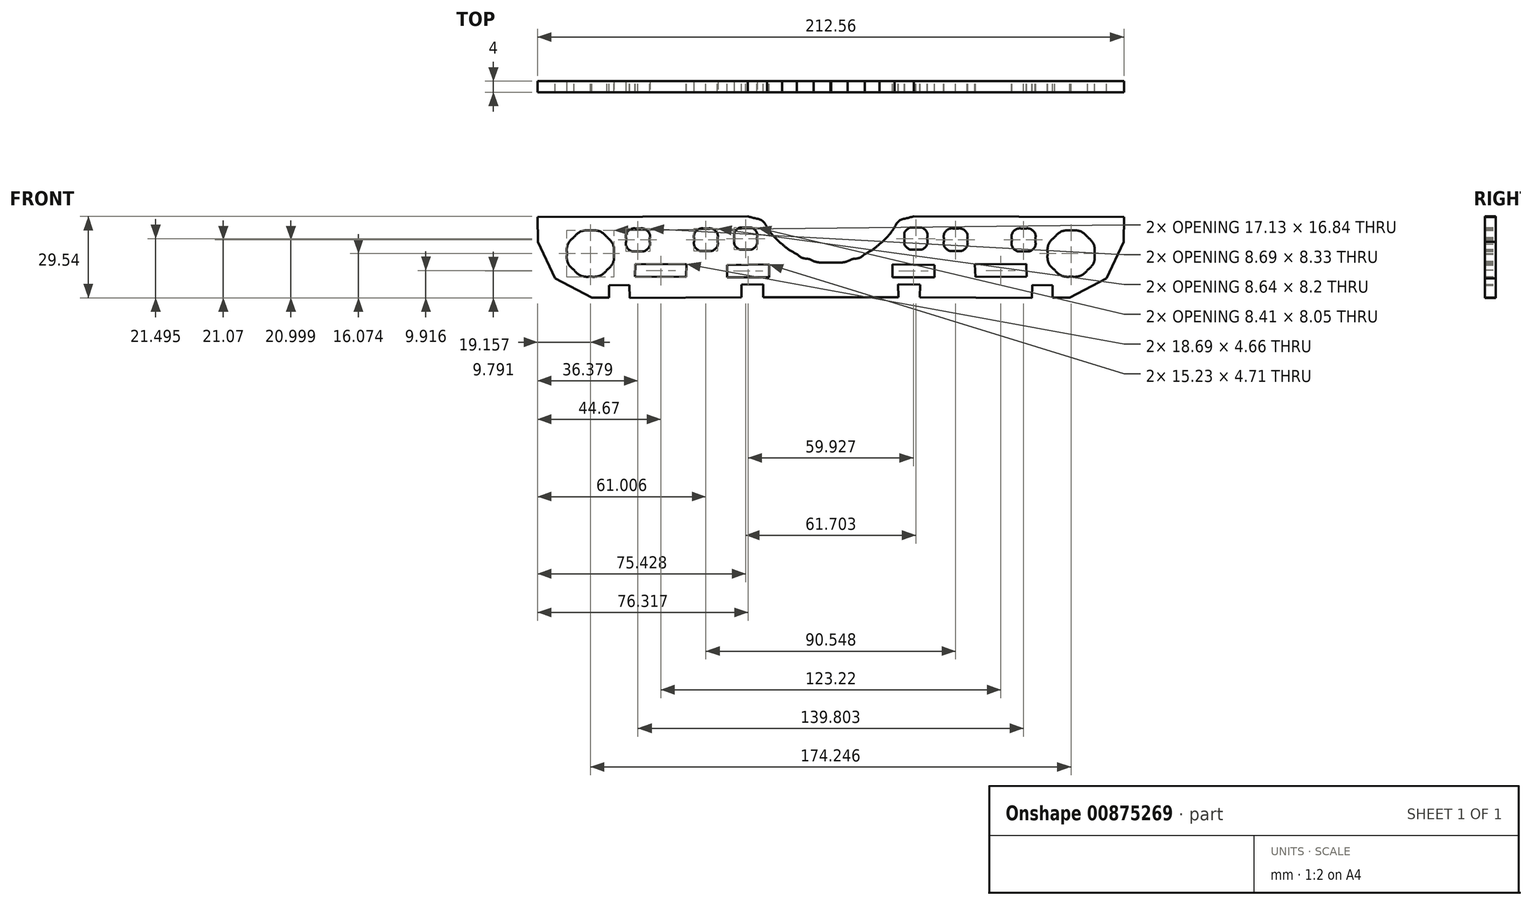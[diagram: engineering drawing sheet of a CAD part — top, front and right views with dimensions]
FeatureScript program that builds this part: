
annotation { "Feature Type Name" : "Feature", "Feature Type Description" : "" }
export const myFeature = defineFeature(function(context is Context, id is Id, definition is map)
    precondition{}
    {
        {
            var Q0;
            Q0=qCreatedBy(makeId("Front.planeOp"),FACE);
            var sketch = newSketch(context, id + "F0", { "sketchPlane" : qUnion([Q0])});
            skLineSegment(sketch, "E0", {"start": v(30.11, 14.14) * mm, "end": v(106.28, 13.9) * mm});
            skLineSegment(sketch, "E1", {"start": v(106.28, 13.9) * mm, "end": v(106.17, 4.91) * mm});
            skLineSegment(sketch, "E2", {"start": v(106.17, 4.91) * mm, "end": v(99.97, -8.35) * mm});
            skLineSegment(sketch, "E3", {"start": v(99.97, -8.35) * mm, "end": v(86.64, -15.33) * mm});
            skLineSegment(sketch, "E4", {"start": v(86.64, -15.33) * mm, "end": v(80.43, -15.33) * mm});
            skLineSegment(sketch, "E5", {"start": v(80.43, -15.33) * mm, "end": v(80.4, -10.83) * mm});
            skLineSegment(sketch, "E6", {"start": v(80.4, -10.83) * mm, "end": v(72.99, -10.77) * mm});
            skLineSegment(sketch, "E7", {"start": v(72.99, -10.77) * mm, "end": v(72.93, -15.4) * mm});
            skLineSegment(sketch, "E8", {"start": v(72.93, -15.4) * mm, "end": v(32.32, -15.13) * mm});
            skLineSegment(sketch, "E9", {"start": v(32.32, -15.13) * mm, "end": v(32.37, -10.57) * mm});
            skLineSegment(sketch, "E10", {"start": v(32.37, -10.57) * mm, "end": v(24.47, -10.45) * mm});
            skLineSegment(sketch, "E11", {"start": v(24.47, -10.45) * mm, "end": v(24.52, -15.13) * mm});
            skLineSegment(sketch, "E12", {"start": v(24.52, -15.13) * mm, "end": v(0, -15.23) * mm});
            skLineSegment(sketch, "E13", {"start": v(22.4, -3.25) * mm, "end": v(37.58, -3.45) * mm});
            skLineSegment(sketch, "E14", {"start": v(37.58, -3.45) * mm, "end": v(37.58, -7.91) * mm});
            skLineSegment(sketch, "E15", {"start": v(37.58, -7.91) * mm, "end": v(22.35, -7.96) * mm});
            skLineSegment(sketch, "E16", {"start": v(22.35, -7.96) * mm, "end": v(22.4, -3.25) * mm});
            skLineSegment(sketch, "E17", {"start": v(52.26, -3.2) * mm, "end": v(70.9, -3.15) * mm});
            skLineSegment(sketch, "E18", {"start": v(70.9, -3.15) * mm, "end": v(70.96, -7.71) * mm});
            skLineSegment(sketch, "E19", {"start": v(70.96, -7.71) * mm, "end": v(52.41, -7.81) * mm});
            skLineSegment(sketch, "E20", {"start": v(52.41, -7.81) * mm, "end": v(52.26, -3.2) * mm});
            skFitSpline(sketch, "E21", {"points": [v(0.1, -2.65) * mm, v(2.27, -2.62) * mm, v(4.38, -2.53) * mm, v(6.16, -2.1) * mm]});
            skFitSpline(sketch, "E22", {"points": [v(6.16, -2.1) * mm, v(8.2, -1.27) * mm, v(10.35, -0.92) * mm, v(12.27, 0.5) * mm]});
            skFitSpline(sketch, "E23", {"points": [v(12.27, 0.5) * mm, v(14.37, 1.56) * mm, v(16.13, 2.79) * mm, v(17.69, 4.11) * mm]});
            skFitSpline(sketch, "E24", {"points": [v(17.69, 4.11) * mm, v(19.77, 5.91) * mm, v(21.55, 7.93) * mm, v(23.1, 10.13) * mm]});
            skFitSpline(sketch, "E25", {"points": [v(23.1, 10.13) * mm, v(24.67, 12.45) * mm, v(27.21, 13.4) * mm, v(30.11, 14.14) * mm]});
            skFitSpline(sketch, "E26", {"points": [v(34.93, 6.1) * mm, v(34.93, 3.94) * mm, v(33.1, 2.2) * mm, v(30.85, 2.2) * mm]});
            skFitSpline(sketch, "E27", {"points": [v(30.85, 2.2) * mm, v(28.6, 2.2) * mm, v(26.78, 3.94) * mm, v(26.78, 6.1) * mm]});
            skFitSpline(sketch, "E28", {"points": [v(26.78, 6.1) * mm, v(26.78, 8.25) * mm, v(28.6, 10) * mm, v(30.85, 10) * mm]});
            skFitSpline(sketch, "E29", {"points": [v(30.85, 10) * mm, v(33.1, 10) * mm, v(34.93, 8.25) * mm, v(34.93, 6.1) * mm]});
            skFitSpline(sketch, "E30", {"points": [v(49.46, 5.67) * mm, v(49.46, 3.48) * mm, v(47.58, 1.7) * mm, v(45.27, 1.7) * mm]});
            skFitSpline(sketch, "E31", {"points": [v(45.27, 1.7) * mm, v(42.96, 1.7) * mm, v(41.1, 3.48) * mm, v(41.1, 5.67) * mm]});
            skFitSpline(sketch, "E32", {"points": [v(41.1, 5.67) * mm, v(41.1, 7.86) * mm, v(42.96, 9.64) * mm, v(45.27, 9.64) * mm]});
            skFitSpline(sketch, "E33", {"points": [v(45.27, 9.64) * mm, v(47.58, 9.64) * mm, v(49.46, 7.86) * mm, v(49.46, 5.67) * mm]});
            skFitSpline(sketch, "E34", {"points": [v(74.11, 5.6) * mm, v(74.11, 3.37) * mm, v(72.23, 1.57) * mm, v(69.9, 1.57) * mm]});
            skFitSpline(sketch, "E35", {"points": [v(69.9, 1.57) * mm, v(67.58, 1.57) * mm, v(65.7, 3.37) * mm, v(65.7, 5.6) * mm]});
            skFitSpline(sketch, "E36", {"points": [v(65.7, 5.6) * mm, v(65.7, 7.83) * mm, v(67.58, 9.63) * mm, v(69.9, 9.63) * mm]});
            skFitSpline(sketch, "E37", {"points": [v(69.9, 9.63) * mm, v(72.23, 9.63) * mm, v(74.11, 7.83) * mm, v(74.11, 5.6) * mm]});
            skFitSpline(sketch, "E38", {"points": [v(95.63, 0.67) * mm, v(95.63, -1.54) * mm, v(94.73, -3.67) * mm, v(93.14, -5.24) * mm]});
            skFitSpline(sketch, "E39", {"points": [v(93.14, -5.24) * mm, v(91.54, -6.8) * mm, v(89.38, -7.69) * mm, v(87.12, -7.69) * mm]});
            skFitSpline(sketch, "E40", {"points": [v(87.12, -7.69) * mm, v(84.87, -7.69) * mm, v(82.7, -6.8) * mm, v(81.11, -5.24) * mm]});
            skFitSpline(sketch, "E41", {"points": [v(81.11, -5.24) * mm, v(79.52, -3.67) * mm, v(78.62, -1.54) * mm, v(78.62, 0.67) * mm]});
            skFitSpline(sketch, "E42", {"points": [v(78.62, 0.67) * mm, v(78.62, 2.9) * mm, v(79.52, 5.02) * mm, v(81.11, 6.59) * mm]});
            skFitSpline(sketch, "E43", {"points": [v(81.11, 6.59) * mm, v(82.7, 8.15) * mm, v(84.87, 9.04) * mm, v(87.12, 9.04) * mm]});
            skFitSpline(sketch, "E44", {"points": [v(87.12, 9.04) * mm, v(89.38, 9.04) * mm, v(91.54, 8.15) * mm, v(93.14, 6.59) * mm]});
            skFitSpline(sketch, "E45", {"points": [v(93.14, 6.59) * mm, v(94.73, 5.02) * mm, v(95.63, 2.9) * mm, v(95.63, 0.67) * mm]});
            skLineSegment(sketch, "E46", {"start": v(0.1, -2.65) * mm, "end": v(0, -2.65) * mm});
            skLineSegment(sketch, "E47", {"start": v(0, -2.65) * mm, "end": v(0, -15.23) * mm});
            skSolve(sketch);
        }
        {
            var Q0;
            Q0 = qSketchRegion(id + "F0", true);
            extrude(context, id + "F1", {"entities" : qUnion([Q0]), "depth" : 4 * mm, "offsetDistance" : 25 * mm});
        }
        {
            var Q0;
            Q0=makeQuery(id+"F1.opExtrude","SWEPT_BODY",BODY,{"disambiguationData":[OSD([sQuery(id+"F0.wireOp",EDGE,"E0"),sQuery(id+"F0.wireOp",EDGE,"E1"),sQuery(id+"F0.wireOp",EDGE,"E2"),sQuery(id+"F0.wireOp",EDGE,"E3"),sQuery(id+"F0.wireOp",EDGE,"E4"),sQuery(id+"F0.wireOp",EDGE,"E5"),sQuery(id+"F0.wireOp",EDGE,"E6"),sQuery(id+"F0.wireOp",EDGE,"E7"),sQuery(id+"F0.wireOp",EDGE,"E8"),sQuery(id+"F0.wireOp",EDGE,"E9"),sQuery(id+"F0.wireOp",EDGE,"E10"),sQuery(id+"F0.wireOp",EDGE,"E11"),sQuery(id+"F0.wireOp",EDGE,"E12"),sQuery(id+"F0.wireOp",EDGE,"E13"),sQuery(id+"F0.wireOp",EDGE,"E14"),sQuery(id+"F0.wireOp",EDGE,"E15"),sQuery(id+"F0.wireOp",EDGE,"E16"),sQuery(id+"F0.wireOp",EDGE,"E17"),sQuery(id+"F0.wireOp",EDGE,"E18"),sQuery(id+"F0.wireOp",EDGE,"E19"),sQuery(id+"F0.wireOp",EDGE,"E20"),sQuery(id+"F0.wireOp",EDGE,"E21"),sQuery(id+"F0.wireOp",EDGE,"E22"),sQuery(id+"F0.wireOp",EDGE,"E23"),sQuery(id+"F0.wireOp",EDGE,"E24"),sQuery(id+"F0.wireOp",EDGE,"E25"),sQuery(id+"F0.wireOp",EDGE,"E26"),sQuery(id+"F0.wireOp",EDGE,"E27"),sQuery(id+"F0.wireOp",EDGE,"E28"),sQuery(id+"F0.wireOp",EDGE,"E29"),sQuery(id+"F0.wireOp",EDGE,"E30"),sQuery(id+"F0.wireOp",EDGE,"E31"),sQuery(id+"F0.wireOp",EDGE,"E32"),sQuery(id+"F0.wireOp",EDGE,"E33"),sQuery(id+"F0.wireOp",EDGE,"E34"),sQuery(id+"F0.wireOp",EDGE,"E35"),sQuery(id+"F0.wireOp",EDGE,"E36"),sQuery(id+"F0.wireOp",EDGE,"E37"),sQuery(id+"F0.wireOp",EDGE,"E38"),sQuery(id+"F0.wireOp",EDGE,"E39"),sQuery(id+"F0.wireOp",EDGE,"E40"),sQuery(id+"F0.wireOp",EDGE,"E41"),sQuery(id+"F0.wireOp",EDGE,"E42"),sQuery(id+"F0.wireOp",EDGE,"E43"),sQuery(id+"F0.wireOp",EDGE,"E44"),sQuery(id+"F0.wireOp",EDGE,"E45"),sQuery(id+"F0.wireOp",EDGE,"E46"),sQuery(id+"F0.wireOp",EDGE,"E47")])]});
            var Q1;
            Q1=qCreatedBy(makeId("Right.planeOp"),FACE);
            mirror(context, id + "F2", {"operationType" : NewBodyOperationType.ADD, "entities" : qUnion([Q0]), "mirrorPlane" : qUnion([Q1])});
        }
    });
